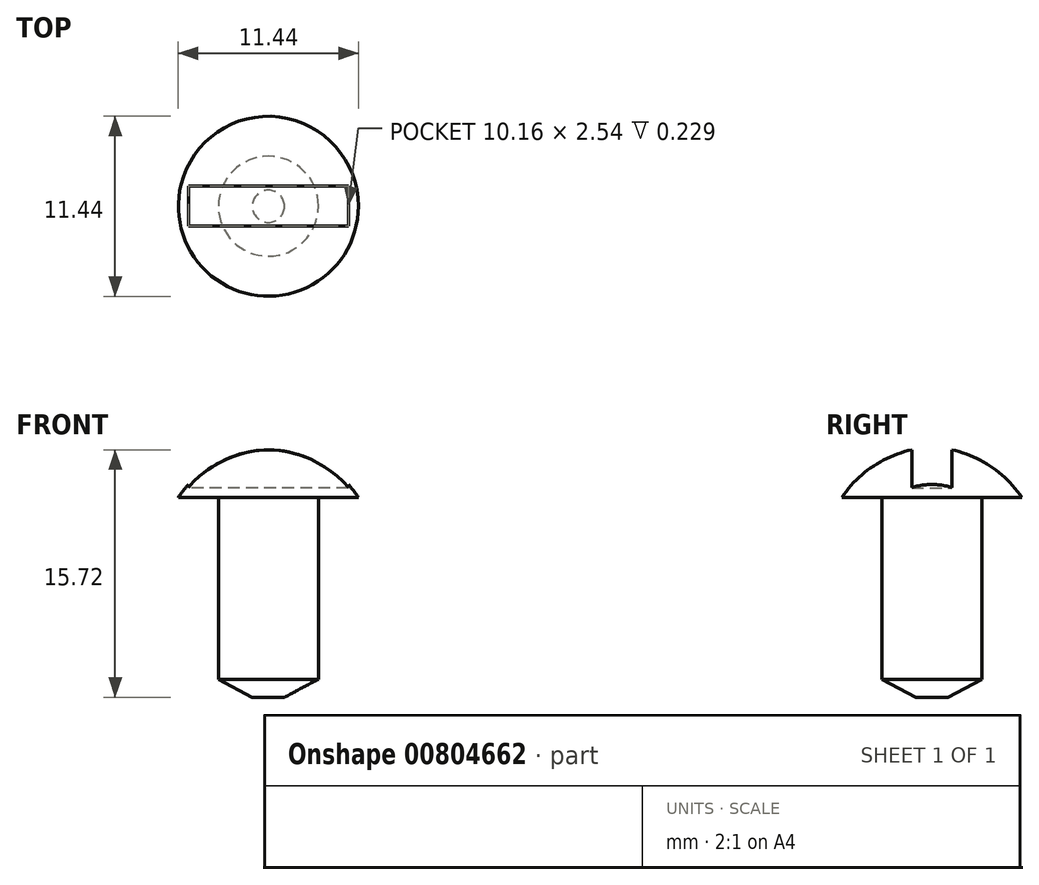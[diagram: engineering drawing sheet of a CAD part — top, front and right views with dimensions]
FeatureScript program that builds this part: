
annotation { "Feature Type Name" : "Feature", "Feature Type Description" : "" }
export const myFeature = defineFeature(function(context is Context, id is Id, definition is map)
    precondition{}
    {
        {
            var Q0;
            Q0=qCreatedBy(makeId("Front.planeOp"),FACE);
            var sketch = newSketch(context, id + "F0", { "sketchPlane" : qUnion([Q0])});
            skLineSegment(sketch, "E0", {"start": v(0, 0) * mm, "end": v(0, 12.54) * mm});
            skLineSegment(sketch, "E1", {"start": v(3.17, 12.7) * mm, "end": v(5.71, 12.7) * mm});
            skArc(sketch, "E2", {"start": v(5.72, 12.7) * mm, "mid": v(3.24, 14.98) * mm, "end": v(0, 15.88) * mm});
            skLineSegment(sketch, "E3", {"start": v(0, 15.88) * mm, "end": v(0, 12.54) * mm});
            skLineSegment(sketch, "E4", {"start": v(1.03, 0) * mm, "end": v(3.18, 1.15) * mm});
            skLineSegment(sketch, "E5", {"start": v(3.17, 12.7) * mm, "end": v(3.17, 1.15) * mm});
            skLineSegment(sketch, "E6", {"start": v(1.03, 0) * mm, "end": v(0, 0) * mm});
            skSolve(sketch);
        }
        {
            var Q0;
            Q0=makeQuery(id+"F0.imprint","IMPRINT",FACE,{"disambiguationData":[TD([[makeQuery(id+"F0.imprint","IMPRINT",EDGE,{"derivedFrom":sQuery(id+"F0.wireOp",EDGE,"E0")}),-1.0]])]});
            var Q1;
            Q1=sQuery(id+"F0.wireOp",EDGE,"E3");
            revolve(context, id + "F1", {"surfaceOperationType" : NewSurfaceOperationType.NEW, "entities" : qUnion([Q0]), "axis" : qUnion([Q1]), "revolveType" : RevolveType.FULL});
        }
        {
            var Q0;
            Q0=qCreatedBy(makeId("Top.planeOp"),FACE);
            cPlane(context, id + "F2", {"entities" : qUnion([Q0]), "cplaneType" : CPlaneType.OFFSET, "offset" : 13.28 * mm, "width" : 152.4 * mm, "height" : 152.4 * mm});
        }
        {
            var Q0;
            Q0=qCreatedBy(id+"F2.planeOp",FACE);
            var sketch = newSketch(context, id + "F3", { "sketchPlane" : qUnion([Q0])});
            skLineSegment(sketch, "E7", {"start": v(0, 0) * mm, "end": v(5.08, 0) * mm});
            skLineSegment(sketch, "E8", {"start": v(5.08, 0) * mm, "end": v(0, 0) * mm, "construction": true});
            skLineSegment(sketch, "E9", {"start": v(0, 0) * mm, "end": v(-5.08, 0) * mm, "construction": true});
            skLineSegment(sketch, "E10", {"start": v(0, 0) * mm, "end": v(0, 1.27) * mm, "construction": true});
            skLineSegment(sketch, "E11", {"start": v(0, 0) * mm, "end": v(0, -1.27) * mm, "construction": true});
            skLineSegment(sketch, "E12", {"start": v(-5.08, 1.27) * mm, "end": v(-5.08, -1.27) * mm});
            skLineSegment(sketch, "E13", {"start": v(-5.08, -1.27) * mm, "end": v(5.08, -1.27) * mm});
            skLineSegment(sketch, "E14", {"start": v(5.08, -1.27) * mm, "end": v(5.08, 1.27) * mm});
            skLineSegment(sketch, "E15", {"start": v(5.08, 1.27) * mm, "end": v(-5.08, 1.27) * mm});
            skSolve(sketch);
        }
        {
            var Q0;
            Q0 = qSketchRegion(id + "F3", true);
            extrude(context, id + "F4", {"entities" : qUnion([Q0]), "operationType" : NewBodyOperationType.REMOVE, "endBound" : BoundingType.THROUGH_ALL, "depth" : 25.4 * mm, "offsetDistance" : 25.4 * mm});
        }
    });
